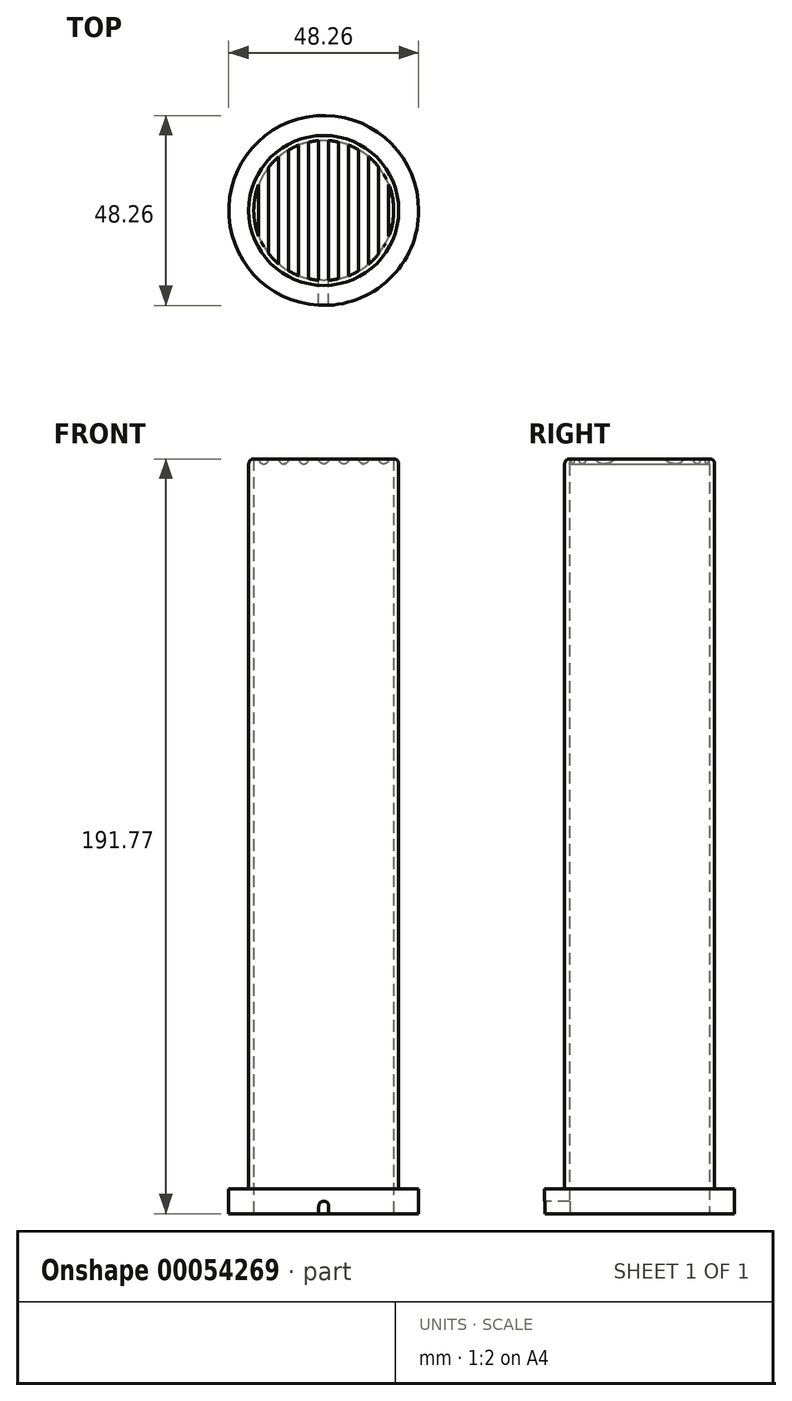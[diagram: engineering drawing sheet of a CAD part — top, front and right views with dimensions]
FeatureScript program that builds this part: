
annotation { "Feature Type Name" : "Feature", "Feature Type Description" : "" }
export const myFeature = defineFeature(function(context is Context, id is Id, definition is map)
    precondition{}
    {
        {
            var Q0;
            Q0=qCreatedBy(makeId("Top.planeOp"),FACE);
            var sketch = newSketch(context, id + "F0", { "sketchPlane" : qUnion([Q0])});
            skCircle(sketch, "E0", {"center": v(0, 0) * mm, "radius": 19.05 * mm});
            skCircle(sketch, "E1", {"center": v(0, 0) * mm, "radius": 17.78 * mm});
            skCircle(sketch, "E2", {"center": v(0, 0) * mm, "radius": 24.13 * mm});
            skPoint(sketch, "E3", {"position": v(0, -17.78) * mm});
            skPoint(sketch, "E4", {"position": v(0, -24.13) * mm});
            skSolve(sketch);
        }
        {
            var Q0;
            Q0=makeQuery(id+"F0.imprint","IMPRINT",FACE,{"disambiguationData":[TD([[makeQuery(id+"F0.imprint","IMPRINT",EDGE,{"derivedFrom":sQuery(id+"F0.wireOp",EDGE,"E0")}),1.0]])]});
            extrude(context, id + "F1", {"entities" : qUnion([Q0]), "depth" : 190.5 * mm});
        }
        {
            var Q0;
            Q0=makeQuery(id+"F0.imprint","IMPRINT",FACE,{"disambiguationData":[TD([[makeQuery(id+"F0.imprint","IMPRINT",EDGE,{"derivedFrom":sQuery(id+"F0.wireOp",EDGE,"E0")}),-1.0]])]});
            extrude(context, id + "F2", {"entities" : qUnion([Q0]), "operationType" : NewBodyOperationType.ADD, "depth" : 6.35 * mm});
        }
        {
            var Q0;
            Q0=makeQuery(id+"F1.opExtrude","CAP_FACE",FACE,{"disambiguationData":[OSD([sQuery(id+"F0.wireOp",EDGE,"E0"),sQuery(id+"F0.wireOp",EDGE,"E1")])],"isStart":false});
            var sketch = newSketch(context, id + "F3", { "sketchPlane" : qUnion([Q0])});
            skLineSegment(sketch, "E5", {"start": v(3.81, -17.37) * mm, "end": v(3.8, 17.37) * mm});
            skLineSegment(sketch, "E6", {"start": v(-1.27, 17.73) * mm, "end": v(-1.27, -17.73) * mm});
            skLineSegment(sketch, "E7", {"start": v(-3.81, 17.37) * mm, "end": v(-3.8, -17.37) * mm});
            skLineSegment(sketch, "E8", {"start": v(-6.35, 16.6) * mm, "end": v(-6.35, -16.6) * mm});
            skLineSegment(sketch, "E9", {"start": v(1.27, 17.73) * mm, "end": v(1.27, -17.73) * mm});
            skLineSegment(sketch, "E10", {"start": v(6.35, 16.6) * mm, "end": v(6.35, -16.6) * mm});
            skLineSegment(sketch, "E11", {"start": v(8.9, 15.4) * mm, "end": v(8.9, -15.4) * mm});
            skLineSegment(sketch, "E12", {"start": v(-8.9, 15.4) * mm, "end": v(-8.89, -15.4) * mm});
            skLineSegment(sketch, "E13", {"start": v(-11.43, 13.62) * mm, "end": v(-11.43, -13.62) * mm});
            skLineSegment(sketch, "E14", {"start": v(-13.97, 11) * mm, "end": v(-13.97, -11) * mm});
            skLineSegment(sketch, "E15", {"start": v(-16.51, 6.6) * mm, "end": v(-16.51, -6.6) * mm});
            skLineSegment(sketch, "E16", {"start": v(11.43, 13.62) * mm, "end": v(11.43, -13.62) * mm});
            skLineSegment(sketch, "E17", {"start": v(13.97, 11) * mm, "end": v(13.97, -11) * mm});
            skLineSegment(sketch, "E18", {"start": v(16.51, 6.6) * mm, "end": v(16.51, -6.6) * mm});
            skPoint(sketch, "E19", {"position": v(0, 19.05) * mm});
            skCircle(sketch, "E20", {"center": v(0, 0) * mm, "radius": 19.05 * mm});
            skCircle(sketch, "E21", {"center": v(0, 0) * mm, "radius": 17.78 * mm});
            skSolve(sketch);
        }
        {
            var Q0;
            Q0=makeQuery(id+"F3.imprint","IMPRINT",FACE,{"disambiguationData":[TD([[makeQuery(id+"F3.imprint","IMPRINT",EDGE,{"derivedFrom":sQuery(id+"F3.wireOp",EDGE,"E20")}),1.0]])]});
            var Q1;
            {var subQ0=sQuery(id+"F3.wireOp",EDGE,"E6");Q1=makeQuery(id+"F3.imprint","IMPRINT",FACE,{"disambiguationData":[TD([[makeQuery(id+"F3.imprint","IMPRINT",EDGE,{"derivedFrom":subQ0}),1.0]])]});}
            var Q2;
            {var subQ0=sQuery(id+"F3.wireOp",EDGE,"E5");Q2=makeQuery(id+"F3.imprint","IMPRINT",FACE,{"disambiguationData":[TD([[makeQuery(id+"F3.imprint","IMPRINT",EDGE,{"derivedFrom":subQ0}),-1.0]])]});}
            var Q3;
            {var subQ0=sQuery(id+"F3.wireOp",EDGE,"E11");Q3=makeQuery(id+"F3.imprint","IMPRINT",FACE,{"disambiguationData":[TD([[makeQuery(id+"F3.imprint","IMPRINT",EDGE,{"derivedFrom":subQ0}),1.0]])]});}
            var Q4;
            {var subQ0=sQuery(id+"F3.wireOp",EDGE,"E17");Q4=makeQuery(id+"F3.imprint","IMPRINT",FACE,{"disambiguationData":[TD([[makeQuery(id+"F3.imprint","IMPRINT",EDGE,{"derivedFrom":subQ0}),1.0]])]});}
            var Q5;
            {var subQ0=sQuery(id+"F3.wireOp",EDGE,"E14");Q5=makeQuery(id+"F3.imprint","IMPRINT",FACE,{"disambiguationData":[TD([[makeQuery(id+"F3.imprint","IMPRINT",EDGE,{"derivedFrom":subQ0}),-1.0]])]});}
            var Q6;
            {var subQ0=sQuery(id+"F3.wireOp",EDGE,"E12");Q6=makeQuery(id+"F3.imprint","IMPRINT",FACE,{"disambiguationData":[TD([[makeQuery(id+"F3.imprint","IMPRINT",EDGE,{"derivedFrom":subQ0}),-1.0]])]});}
            var Q7;
            {var subQ0=sQuery(id+"F3.wireOp",EDGE,"E7");Q7=makeQuery(id+"F3.imprint","IMPRINT",FACE,{"disambiguationData":[TD([[makeQuery(id+"F3.imprint","IMPRINT",EDGE,{"derivedFrom":subQ0}),-1.0]])]});}
            extrude(context, id + "F4", {"entities" : qUnion([Q0, Q1, Q2, Q3, Q4, Q5, Q6, Q7]), "operationType" : NewBodyOperationType.ADD, "depth" : 1.27 * mm});
        }
        {
            var Q0;
            Q0=makeQuery(id+"F0.imprint","IMPRINT",FACE,{"disambiguationData":[TD([[makeQuery(id+"F0.imprint","IMPRINT",EDGE,{"derivedFrom":sQuery(id+"F0.wireOp",EDGE,"E0")}),-1.0]])]});
            var sketch = newSketch(context, id + "F5", { "sketchPlane" : qUnion([Q0])});
            skLineSegment(sketch, "E22.bottom", {"start": v(-1.27, -24.13) * mm, "end": v(1.27, -24.13) * mm});
            skLineSegment(sketch, "E22.top", {"start": v(-1.27, -17.42) * mm, "end": v(1.27, -17.42) * mm});
            skLineSegment(sketch, "E22.left", {"start": v(-1.27, -24.13) * mm, "end": v(-1.27, -17.42) * mm});
            skLineSegment(sketch, "E22.right", {"start": v(1.27, -24.13) * mm, "end": v(1.27, -17.42) * mm});
            skSolve(sketch);
        }
        {
            var Q0;
            Q0 = qSketchRegion(id + "F5", true);
            extrude(context, id + "F6", {"entities" : qUnion([Q0]), "operationType" : NewBodyOperationType.REMOVE, "depth" : 3.17 * mm});
        }
        {
            var Q0;
            Q0=makeQuery(id+"F4.opExtrude","CAP_EDGE",EDGE,{"disambiguationData":[OSD([sQuery(id+"F3.wireOp",EDGE,"E20")])],"isStart":false});
            var Q1;
            Q1=makeQuery(id+"F4.opExtrude","CAP_EDGE",EDGE,{"disambiguationData":[OSD([sQuery(id+"F3.wireOp",EDGE,"E14")])],"isStart":true});
            var Q2;
            Q2=makeQuery(id+"F4.opExtrude","CAP_EDGE",EDGE,{"disambiguationData":[OSD([sQuery(id+"F3.wireOp",EDGE,"E12")])],"isStart":true});
            var Q3;
            Q3=makeQuery(id+"F4.opExtrude","CAP_EDGE",EDGE,{"disambiguationData":[OSD([sQuery(id+"F3.wireOp",EDGE,"E7")])],"isStart":true});
            var Q4;
            Q4=makeQuery(id+"F4.opExtrude","CAP_EDGE",EDGE,{"disambiguationData":[OSD([sQuery(id+"F3.wireOp",EDGE,"E9")])],"isStart":true});
            var Q5;
            Q5=makeQuery(id+"F4.opExtrude","CAP_EDGE",EDGE,{"disambiguationData":[OSD([sQuery(id+"F3.wireOp",EDGE,"E10")])],"isStart":true});
            var Q6;
            Q6=makeQuery(id+"F4.opExtrude","CAP_EDGE",EDGE,{"disambiguationData":[OSD([sQuery(id+"F3.wireOp",EDGE,"E16")])],"isStart":true});
            var Q7;
            Q7=makeQuery(id+"F4.opExtrude","CAP_EDGE",EDGE,{"disambiguationData":[OSD([sQuery(id+"F3.wireOp",EDGE,"E18")])],"isStart":true});
            var Q8;
            Q8=makeQuery(id+"F4.opExtrude","CAP_EDGE",EDGE,{"disambiguationData":[OSD([sQuery(id+"F3.wireOp",EDGE,"E15")])],"isStart":true});
            var Q9;
            Q9=makeQuery(id+"F4.opExtrude","CAP_EDGE",EDGE,{"disambiguationData":[OSD([sQuery(id+"F3.wireOp",EDGE,"E13")])],"isStart":true});
            var Q10;
            Q10=makeQuery(id+"F4.opExtrude","CAP_EDGE",EDGE,{"disambiguationData":[OSD([sQuery(id+"F3.wireOp",EDGE,"E8")])],"isStart":true});
            var Q11;
            Q11=makeQuery(id+"F4.opExtrude","CAP_EDGE",EDGE,{"disambiguationData":[OSD([sQuery(id+"F3.wireOp",EDGE,"E6")])],"isStart":true});
            var Q12;
            Q12=makeQuery(id+"F4.opExtrude","CAP_EDGE",EDGE,{"disambiguationData":[OSD([sQuery(id+"F3.wireOp",EDGE,"E5")])],"isStart":true});
            var Q13;
            Q13=makeQuery(id+"F4.opExtrude","CAP_EDGE",EDGE,{"disambiguationData":[OSD([sQuery(id+"F3.wireOp",EDGE,"E17")])],"isStart":true});
            var Q14;
            Q14=makeQuery(id+"F4.opExtrude","CAP_EDGE",EDGE,{"disambiguationData":[OSD([sQuery(id+"F3.wireOp",EDGE,"E11")])],"isStart":true});
            var Q15;
            Q15=makeQuery(id+"F6.boolean.opBoolean","COPY",EDGE,{"derivedFrom":makeQuery(id+"F6.opExtrude","CAP_EDGE",EDGE,{"disambiguationData":[OSD([sQuery(id+"F5.wireOp",EDGE,"E22.left")])],"isStart":false})});
            var Q16;
            Q16=makeQuery(id+"F6.boolean.opBoolean","COPY",EDGE,{"derivedFrom":makeQuery(id+"F6.opExtrude","CAP_EDGE",EDGE,{"disambiguationData":[OSD([sQuery(id+"F5.wireOp",EDGE,"E22.right")])],"isStart":false})});
            fillet(context, id + "F7", {"entities" : qUnion([Q0, Q1, Q2, Q3, Q4, Q5, Q6, Q7, Q8, Q9, Q10, Q11, Q12, Q13, Q14, Q15, Q16]), "radius" : 1.27 * mm, "tangentPropagation" : true, "allowEdgeOverflow" : false});
        }
    });
